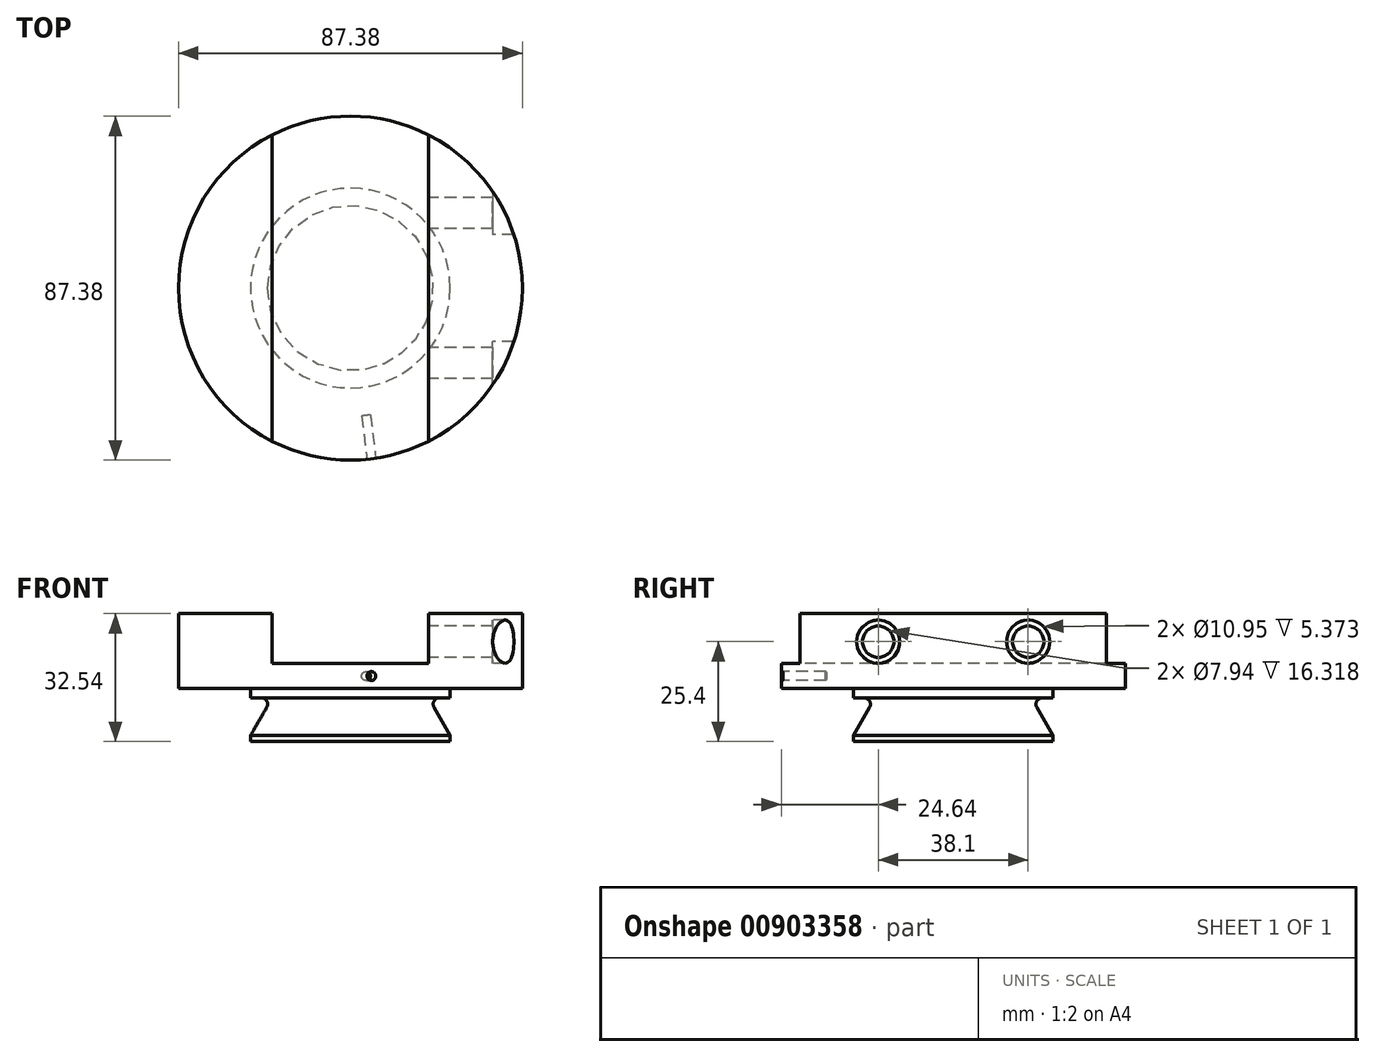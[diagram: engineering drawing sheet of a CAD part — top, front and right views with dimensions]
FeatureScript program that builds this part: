
annotation { "Feature Type Name" : "Feature", "Feature Type Description" : "" }
export const myFeature = defineFeature(function(context is Context, id is Id, definition is map)
    precondition{}
    {
        {
            var Q0;
            Q0=qCreatedBy(makeId("Front.planeOp"),FACE);
            var sketch = newSketch(context, id + "F0", { "sketchPlane" : qUnion([Q0])});
            skLineSegment(sketch, "E0", {"start": v(25.37, 0) * mm, "end": v(25.37, 1.59) * mm});
            skLineSegment(sketch, "E1", {"start": v(25.37, 1.59) * mm, "end": v(19.87, 11.13) * mm});
            skLineSegment(sketch, "E2", {"start": v(19.87, 11.13) * mm, "end": v(25.37, 11.13) * mm});
            skLineSegment(sketch, "E3", {"start": v(25.37, 11.13) * mm, "end": v(25.37, 13.49) * mm});
            skLineSegment(sketch, "E4", {"start": v(25.37, 0) * mm, "end": v(0, 0) * mm});
            skLineSegment(sketch, "E5", {"start": v(0, 0) * mm, "end": v(0, 13.49) * mm});
            skLineSegment(sketch, "E6", {"start": v(0, 13.49) * mm, "end": v(25.37, 13.49) * mm});
            skSolve(sketch);
        }
        {
            var Q0;
            Q0 = qSketchRegion(id + "F0", true);
            var Q1;
            Q1=sQuery(id+"F0.wireOp",EDGE,"E5");
            revolve(context, id + "F1", {"surfaceOperationType" : NewSurfaceOperationType.NEW, "entities" : qUnion([Q0]), "axis" : qUnion([Q1]), "revolveType" : RevolveType.FULL});
        }
        {
            var Q0;
            Q0=makeQuery(id+"F1.opRevolve","SWEPT_FACE",FACE,{"disambiguationData":[OSD([sQuery(id+"F0.wireOp",EDGE,"E6")])]});
            cPlane(context, id + "F2", {"entities" : qUnion([Q0]), "cplaneType" : CPlaneType.OFFSET, "offset" : 0 * mm, "width" : 152.4 * mm, "height" : 152.4 * mm});
        }
        {
            var Q0;
            Q0=qCreatedBy(id+"F2.planeOp",FACE);
            var sketch = newSketch(context, id + "F3", { "sketchPlane" : qUnion([Q0])});
            skCircle(sketch, "E7", {"center": v(0, 0) * mm, "radius": 43.69 * mm});
            skSolve(sketch);
        }
        {
            var Q0;
            Q0=makeQuery(id+"F3.imprint","IMPRINT",FACE,{"disambiguationData":[TD([[makeQuery(id+"F3.imprint","IMPRINT",EDGE,{"derivedFrom":sQuery(id+"F3.wireOp",EDGE,"E7")}),1.0]])]});
            extrude(context, id + "F4", {"entities" : qUnion([Q0]), "operationType" : NewBodyOperationType.ADD, "depth" : 19.05 * mm, "offsetDistance" : 25.4 * mm});
        }
        {
            var Q0;
            Q0=makeQuery(id+"F1.opRevolve","SWEPT_EDGE",EDGE,{"disambiguationData":[OSD([sQuery(id+"F0.wireOp",EDGE,"E1"),sQuery(id+"F0.wireOp",EDGE,"E2")])]});
            fillet(context, id + "F5", {"entities" : qUnion([Q0]), "radius" : 1.59 * mm, "tangentPropagation" : true, "allowEdgeOverflow" : false});
        }
        {
            var Q0;
            Q0=qCreatedBy(makeId("Front.planeOp"),FACE);
            cPlane(context, id + "F6", {"entities" : qUnion([Q0]), "cplaneType" : CPlaneType.OFFSET, "offset" : 0 * mm, "width" : 152.4 * mm, "height" : 152.4 * mm});
        }
        {
            var Q0;
            Q0=qCreatedBy(id+"F6.planeOp",FACE);
            var sketch = newSketch(context, id + "F7", { "sketchPlane" : qUnion([Q0])});
            skLineSegment(sketch, "E8.0", {"start": v(-19.84, 32.54) * mm, "end": v(19.84, 32.54) * mm});
            skLineSegment(sketch, "E9.0", {"start": v(-19.84, 19.84) * mm, "end": v(19.84, 19.84) * mm});
            skLineSegment(sketch, "E10", {"start": v(-19.84, 32.54) * mm, "end": v(-19.84, 19.84) * mm});
            skLineSegment(sketch, "E11", {"start": v(19.84, 32.54) * mm, "end": v(19.84, 19.84) * mm});
            skSolve(sketch);
        }
        {
            var Q0;
            Q0=makeQuery(id+"F7.imprint","IMPRINT",FACE,{"disambiguationData":[TD([[makeQuery(id+"F7.imprint","IMPRINT",EDGE,{"derivedFrom":sQuery(id+"F7.wireOp",EDGE,"E8.0")}),-1.0]])]});
            extrude(context, id + "F8", {"entities" : qUnion([Q0]), "operationType" : NewBodyOperationType.REMOVE, "endBound" : BoundingType.THROUGH_ALL, "oppositeDirection" : true, "depth" : 25.4 * mm, "offsetDistance" : 25.4 * mm, "hasSecondDirection" : true, "secondDirectionBound" : BoundingType.THROUGH_ALL, "secondDirectionOppositeDirection" : false, "secondDirectionDepth" : 25.4 * mm});
        }
        {
            var Q0;
            Q0=qCreatedBy(makeId("Right.planeOp"),FACE);
            cPlane(context, id + "F9", {"entities" : qUnion([Q0]), "cplaneType" : CPlaneType.OFFSET, "offset" : 43.69 * mm, "width" : 152.4 * mm, "height" : 152.4 * mm});
        }
        {
            var Q0;
            Q0=qCreatedBy(id+"F9.planeOp",FACE);
            var sketch = newSketch(context, id + "F10", { "sketchPlane" : qUnion([Q0])});
            skPoint(sketch, "E12", {"position": v(-19.05, 25.4) * mm});
            skPoint(sketch, "E13", {"position": v(19.05, 25.4) * mm});
            skSolve(sketch);
        }
        {
            var Q0;
            Q0=sQuery(id+"F10.wireOp",VERTEX,"E12");
            var Q1;
            Q1=sQuery(id+"F10.wireOp",VERTEX,"E13");
            var Q2;
            Q2=makeQuery(id+"F1.opRevolve","SWEPT_BODY",BODY,{"disambiguationData":[OSD([sQuery(id+"F0.wireOp",EDGE,"E0"),sQuery(id+"F0.wireOp",EDGE,"E1"),sQuery(id+"F0.wireOp",EDGE,"E2"),sQuery(id+"F0.wireOp",EDGE,"E3"),sQuery(id+"F0.wireOp",EDGE,"E4"),sQuery(id+"F0.wireOp",EDGE,"E5"),sQuery(id+"F0.wireOp",EDGE,"E6")])]});
            hole(context, id + "F11", {"style" : HoleStyle.C_BORE, "endStyle" : HoleEndStyle.BLIND, "holeDiameter" : 7.94 * mm, "cBoreDiameter" : 10.95 * mm, "cBoreDepth" : 0 * mm, "majorDiameter" : 9.52 * mm, "holeDepth" : 19.09 * mm, "tappedDepth" : 14.33 * mm, "tapClearance" : 3, "locations" : qUnion([Q0, Q1]), "scope" : qUnion([Q2]), "startStyle" : HoleStartStyle.PART});
        }
        {
            var Q0;
            Q0=makeQuery(id+"F8.boolean.opBoolean","COPY",FACE,{"derivedFrom":makeQuery(id+"F8.opExtrude","SWEPT_FACE",FACE,{"disambiguationData":[OSD([sQuery(id+"F7.wireOp",EDGE,"E9.0")])]})});
            cPlane(context, id + "F12", {"entities" : qUnion([Q0]), "cplaneType" : CPlaneType.OFFSET, "offset" : 3.17 * mm, "oppositeDirection" : true, "width" : 152.4 * mm, "height" : 152.4 * mm});
        }
        {
            var Q0;
            Q0=qCreatedBy(id+"F12.planeOp",FACE);
            var sketch = newSketch(context, id + "F13", { "sketchPlane" : qUnion([Q0])});
            skLineSegment(sketch, "E14", {"start": v(0, 0) * mm, "end": v(5.32, -43.36) * mm});
            skLineSegment(sketch, "E15", {"start": v(5.32, -43.36) * mm, "end": v(35.33, -39.68) * mm});
            skSolve(sketch);
        }
        {
            var Q0;
            Q0=sQuery(id+"F13.wireOp",EDGE,"E15");
            cPlane(context, id + "F14", {"entities" : qUnion([Q0]), "cplaneType" : CPlaneType.LINE_ANGLE, "offset" : 25.4 * mm, "angle" : 0 * degree, "width" : 152.4 * mm, "height" : 152.4 * mm});
        }
        {
            var Q0;
            Q0=qCreatedBy(id+"F14.planeOp",FACE);
            var sketch = newSketch(context, id + "F15", { "sketchPlane" : qUnion([Q0])});
            skPoint(sketch, "E16.0", {"position": v(0, 16.66) * mm});
            skCircle(sketch, "E17", {"center": v(0, 16.66) * mm, "radius": 1.13 * mm});
            skSolve(sketch);
        }
        {
            var Q0;
            Q0=makeQuery(id+"F15.imprint","IMPRINT",FACE,{"disambiguationData":[TD([[makeQuery(id+"F15.imprint","IMPRINT",EDGE,{"derivedFrom":sQuery(id+"F15.wireOp",EDGE,"E17")}),1.0]])]});
            extrude(context, id + "F16", {"entities" : qUnion([Q0]), "operationType" : NewBodyOperationType.REMOVE, "depth" : 11.1 * mm, "offsetDistance" : 25.4 * mm});
        }
    });
